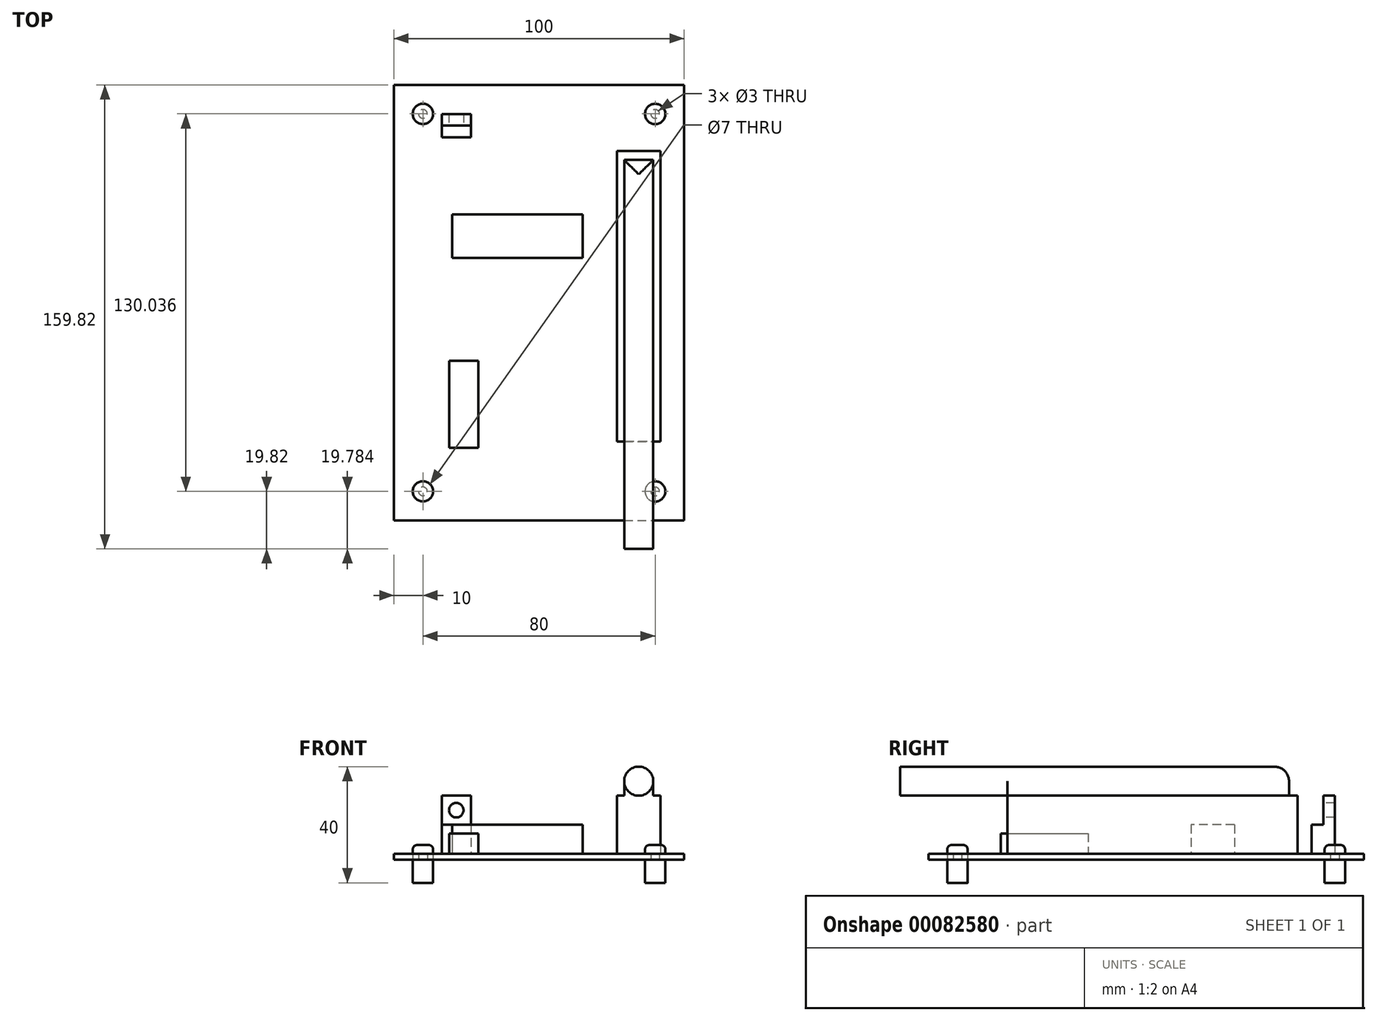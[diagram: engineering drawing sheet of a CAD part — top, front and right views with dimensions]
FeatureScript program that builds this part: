
annotation { "Feature Type Name" : "Feature", "Feature Type Description" : "" }
export const myFeature = defineFeature(function(context is Context, id is Id, definition is map)
    precondition{}
    {
        {
            var Q0;
            Q0=qCreatedBy(makeId("Top.planeOp"),FACE);
            var sketch = newSketch(context, id + "F0", { "sketchPlane" : qUnion([Q0])});
            skLineSegment(sketch, "E0.bottom", {"start": v(0, 0) * mm, "end": v(100, 0) * mm});
            skLineSegment(sketch, "E0.top", {"start": v(0, 150) * mm, "end": v(100, 150) * mm});
            skLineSegment(sketch, "E0.left", {"start": v(0, 0) * mm, "end": v(0, 150) * mm});
            skLineSegment(sketch, "E0.right", {"start": v(100, 0) * mm, "end": v(100, 150) * mm});
            skCircle(sketch, "E1", {"center": v(10, 10) * mm, "radius": 1.5 * mm});
            skCircle(sketch, "E2", {"center": v(10, 140) * mm, "radius": 1.5 * mm});
            skCircle(sketch, "E3", {"center": v(90, 9.96) * mm, "radius": 1.5 * mm});
            skCircle(sketch, "E4", {"center": v(90, 140) * mm, "radius": 1.5 * mm});
            skCircle(sketch, "E5", {"center": v(10, 10) * mm, "radius": 3.5 * mm});
            skSolve(sketch);
        }
        {
            var Q0;
            Q0=makeQuery(id+"F0.imprint","IMPRINT",FACE,{"disambiguationData":[TD([[makeQuery(id+"F0.imprint","IMPRINT",EDGE,{"derivedFrom":sQuery(id+"F0.wireOp",EDGE,"E0.bottom")}),1.0]])]});
            var Q1;
            Q1=makeQuery(id+"F0.imprint","IMPRINT",FACE,{"disambiguationData":[TD([[makeQuery(id+"F0.imprint","IMPRINT",EDGE,{"derivedFrom":sQuery(id+"F0.wireOp",EDGE,"E1")}),-1.0]])]});
            extrude(context, id + "F1", {"entities" : qUnion([Q0, Q1]), "depth" : 2 * mm});
        }
        {
            var Q0;
            Q0=makeQuery(id+"F1.opExtrude","CAP_FACE",FACE,{"disambiguationData":[OSD([sQuery(id+"F0.wireOp",EDGE,"E0.bottom"),sQuery(id+"F0.wireOp",EDGE,"E0.top"),sQuery(id+"F0.wireOp",EDGE,"E0.left"),sQuery(id+"F0.wireOp",EDGE,"E0.right"),sQuery(id+"F0.wireOp",EDGE,"E1"),sQuery(id+"F0.wireOp",EDGE,"E2"),sQuery(id+"F0.wireOp",EDGE,"E3"),sQuery(id+"F0.wireOp",EDGE,"E4")])],"isStart":false});
            var sketch = newSketch(context, id + "F2", { "sketchPlane" : qUnion([Q0])});
            skLineSegment(sketch, "E6.bottom", {"start": v(19.05, 24.96) * mm, "end": v(29.05, 24.96) * mm});
            skLineSegment(sketch, "E6.top", {"start": v(19.05, 54.96) * mm, "end": v(29.05, 54.96) * mm});
            skLineSegment(sketch, "E6.left", {"start": v(19.05, 24.96) * mm, "end": v(19.05, 54.96) * mm});
            skLineSegment(sketch, "E6.right", {"start": v(29.05, 24.96) * mm, "end": v(29.05, 54.96) * mm});
            skLineSegment(sketch, "E7.bottom", {"start": v(20, 105.4) * mm, "end": v(65, 105.4) * mm});
            skLineSegment(sketch, "E7.top", {"start": v(20, 90.4) * mm, "end": v(65, 90.4) * mm});
            skLineSegment(sketch, "E7.left", {"start": v(20, 105.4) * mm, "end": v(20, 90.4) * mm});
            skLineSegment(sketch, "E7.right", {"start": v(65, 105.4) * mm, "end": v(65, 90.4) * mm});
            skLineSegment(sketch, "E8.bottom", {"start": v(16.48, 139.98) * mm, "end": v(26.48, 139.98) * mm});
            skLineSegment(sketch, "E8.top", {"start": v(16.48, 131.98) * mm, "end": v(26.48, 131.98) * mm});
            skLineSegment(sketch, "E8.left", {"start": v(16.48, 139.98) * mm, "end": v(16.48, 131.98) * mm});
            skLineSegment(sketch, "E8.right", {"start": v(26.48, 139.98) * mm, "end": v(26.48, 131.98) * mm});
            skLineSegment(sketch, "E9.top", {"start": v(16.48, 135.98) * mm, "end": v(26.48, 135.98) * mm});
            skLineSegment(sketch, "E9.left", {"start": v(16.48, 139.98) * mm, "end": v(16.48, 135.98) * mm});
            skLineSegment(sketch, "E9.right", {"start": v(26.48, 139.98) * mm, "end": v(26.48, 135.98) * mm});
            skLineSegment(sketch, "E10.bottom", {"start": v(91.82, 127.18) * mm, "end": v(76.82, 127.18) * mm});
            skLineSegment(sketch, "E10.top", {"start": v(91.82, 27.18) * mm, "end": v(76.82, 27.18) * mm});
            skLineSegment(sketch, "E10.left", {"start": v(91.82, 127.18) * mm, "end": v(91.82, 27.18) * mm});
            skLineSegment(sketch, "E10.right", {"start": v(76.82, 127.18) * mm, "end": v(76.82, 27.18) * mm});
            skSolve(sketch);
        }
        {
            var Q0;
            Q0=makeQuery(id+"F2.imprint","IMPRINT",FACE,{"disambiguationData":[TD([[makeQuery(id+"F2.imprint","IMPRINT",EDGE,{"derivedFrom":sQuery(id+"F2.wireOp",EDGE,"E7.bottom")}),-1.0]])]});
            var Q1;
            Q1=makeQuery(id+"F2.imprint","IMPRINT",FACE,{"disambiguationData":[TD([[makeQuery(id+"F2.imprint","IMPRINT",EDGE,{"derivedFrom":sQuery(id+"F2.wireOp",EDGE,"E8.top")}),1.0]])]});
            var Q2;
            Q2=makeQuery(id+"F2.imprint","IMPRINT",FACE,{"disambiguationData":[TD([[makeQuery(id+"F2.imprint","IMPRINT",EDGE,{"derivedFrom":sQuery(id+"F2.wireOp",EDGE,"E8.bottom")}),-1.0]])]});
            var Q3;
            Q3=makeQuery(id+"F2.imprint","IMPRINT",FACE,{"disambiguationData":[TD([[makeQuery(id+"F2.imprint","IMPRINT",EDGE,{"derivedFrom":sQuery(id+"F2.wireOp",EDGE,"E10.bottom")}),1.0]])]});
            extrude(context, id + "F3", {"entities" : qUnion([Q0, Q1, Q2, Q3]), "depth" : 10 * mm});
        }
        {
            var Q0;
            Q0=makeQuery(id+"F2.imprint","IMPRINT",FACE,{"disambiguationData":[TD([[makeQuery(id+"F2.imprint","IMPRINT",EDGE,{"derivedFrom":sQuery(id+"F2.wireOp",EDGE,"E8.bottom")}),-1.0]])]});
            extrude(context, id + "F4", {"entities" : qUnion([Q0]), "operationType" : NewBodyOperationType.ADD, "depth" : 20 * mm});
        }
        {
            var Q0;
            Q0=makeQuery(id+"F2.imprint","IMPRINT",FACE,{"disambiguationData":[TD([[makeQuery(id+"F2.imprint","IMPRINT",EDGE,{"derivedFrom":sQuery(id+"F2.wireOp",EDGE,"E6.bottom")}),1.0]])]});
            extrude(context, id + "F5", {"entities" : qUnion([Q0]), "depth" : 7 * mm});
        }
        {
            var Q0;
            Q0=makeQuery(id+"F4.opExtrude","SWEPT_FACE",FACE,{"disambiguationData":[OSD([sQuery(id+"F2.wireOp",EDGE,"E9.top")])]});
            var sketch = newSketch(context, id + "F6", { "sketchPlane" : qUnion([Q0])});
            skCircle(sketch, "E11", {"center": v(21.48, 17) * mm, "radius": 2.5 * mm});
            skPoint(sketch, "E11.centerSnap0", {"position": v(26.48, 17) * mm});
            skPoint(sketch, "E11.centerSnap1", {"position": v(21.48, 22) * mm});
            skSolve(sketch);
        }
        {
            var Q0;
            Q0=qSketchRegion(id+"F6",true);
            extrude(context, id + "F7", {"entities" : qUnion([Q0]), "operationType" : NewBodyOperationType.REMOVE, "oppositeDirection" : true, "depth" : 25 * mm});
        }
        {
            var Q0;
            Q0=makeQuery(id+"F3.opExtrude","CAP_FACE",FACE,{"disambiguationData":[OSD([sQuery(id+"F2.wireOp",EDGE,"E10.bottom"),sQuery(id+"F2.wireOp",EDGE,"E10.top"),sQuery(id+"F2.wireOp",EDGE,"E10.left"),sQuery(id+"F2.wireOp",EDGE,"E10.right")])],"isStart":false});
            extrude(context, id + "F8", {"entities" : qUnion([Q0]), "operationType" : NewBodyOperationType.ADD, "depth" : 10 * mm});
        }
        {
            var Q0;
            Q0=makeQuery(id+"F8.opExtrude","CAP_FACE",FACE,{"disambiguationData":[OSD([sQuery(id+"F2.wireOp",EDGE,"E10.bottom"),sQuery(id+"F2.wireOp",EDGE,"E10.top"),sQuery(id+"F2.wireOp",EDGE,"E10.left"),sQuery(id+"F2.wireOp",EDGE,"E10.right")])],"isStart":false});
            var sketch = newSketch(context, id + "F9", { "sketchPlane" : qUnion([Q0])});
            skLineSegment(sketch, "E12.bottom", {"start": v(79.32, 124.18) * mm, "end": v(89.32, 124.18) * mm});
            skLineSegment(sketch, "E12.top", {"start": v(79.32, 30.18) * mm, "end": v(89.32, 30.18) * mm});
            skLineSegment(sketch, "E12.left", {"start": v(79.32, 124.18) * mm, "end": v(79.32, 30.18) * mm});
            skLineSegment(sketch, "E12.right", {"start": v(89.32, 124.18) * mm, "end": v(89.32, 30.18) * mm});
            skLineSegment(sketch, "E13", {"start": v(79.32, 124.18) * mm, "end": v(76.82, 127.18) * mm});
            skLineSegment(sketch, "E14", {"start": v(89.32, 124.18) * mm, "end": v(91.82, 127.18) * mm});
            skLineSegment(sketch, "E15", {"start": v(89.32, 30.18) * mm, "end": v(91.82, 27.18) * mm});
            skLineSegment(sketch, "E16", {"start": v(76.82, 27.18) * mm, "end": v(79.32, 30.18) * mm});
            skLineSegment(sketch, "E17.bottom", {"start": v(79.32, 124.18) * mm, "end": v(76.82, 124.18) * mm});
            skLineSegment(sketch, "E17.top", {"start": v(79.32, 127.18) * mm, "end": v(76.82, 127.18) * mm});
            skLineSegment(sketch, "E17.left", {"start": v(79.32, 124.18) * mm, "end": v(79.32, 127.18) * mm});
            skLineSegment(sketch, "E17.right", {"start": v(76.82, 124.18) * mm, "end": v(76.82, 127.18) * mm});
            skSolve(sketch);
        }
        {
            var Q0;
            Q0=makeQuery(id+"F9.imprint","IMPRINT",FACE,{"disambiguationData":[TD([[makeQuery(id+"F9.imprint","IMPRINT",EDGE,{"derivedFrom":sQuery(id+"F9.wireOp",EDGE,"E12.bottom")}),-1.0]])]});
            extrude(context, id + "F10", {"entities" : qUnion([Q0]), "operationType" : NewBodyOperationType.ADD, "depth" : 10 * mm});
        }
        {
            var Q0;
            Q0=makeQuery(id+"F10.opExtrude","CAP_EDGE",EDGE,{"disambiguationData":[OSD([sQuery(id+"F9.wireOp",EDGE,"E12.right")])],"isStart":false});
            var Q1;
            Q1=makeQuery(id+"F10.opExtrude","CAP_EDGE",EDGE,{"disambiguationData":[OSD([sQuery(id+"F9.wireOp",EDGE,"E12.left")])],"isStart":false});
            var Q2;
            Q2=makeQuery(id+"F10.opExtrude","CAP_EDGE",EDGE,{"disambiguationData":[OSD([sQuery(id+"F9.wireOp",EDGE,"E12.bottom")])],"isStart":false});
            fillet(context, id + "F11", {"entities" : qUnion([Q0, Q1, Q2]), "radius" : 5 * mm, "tangentPropagation" : true, "allowEdgeOverflow" : false});
        }
        {
            var Q0;
            Q0=makeQuery(id+"F10.opExtrude","SWEPT_FACE",FACE,{"disambiguationData":[OSD([sQuery(id+"F9.wireOp",EDGE,"E12.top")])]});
            var Q1;
            Q1=makeQuery(id+"F1.opExtrude","SWEPT_FACE",FACE,{"disambiguationData":[OSD([sQuery(id+"F0.wireOp",EDGE,"E0.bottom")])]});
            extrude(context, id + "F12", {"entities" : qUnion([Q0]), "operationType" : NewBodyOperationType.ADD, "endBoundEntityFace" : qUnion([Q1]), "depth" : 40 * mm});
        }
        {
            var Q0;
            Q0=makeQuery(id+"F12.boolean.opBoolean","SPLIT",EDGE,{"derivedFrom":makeQuery(id+"F12.opExtrude","SWEPT_EDGE",EDGE,{"disambiguationData":[OSD([sQuery(id+"F9.wireOp",EDGE,"E12.top"),sQuery(id+"F9.wireOp",EDGE,"E12.right"),sQuery(id+"F9.wireOp",EDGE,"E15")])]})});
            var Q1;
            Q1=makeQuery(id+"F12.boolean.opBoolean","SPLIT",EDGE,{"derivedFrom":makeQuery(id+"F12.opExtrude","SWEPT_EDGE",EDGE,{"disambiguationData":[OSD([sQuery(id+"F9.wireOp",EDGE,"E12.top"),sQuery(id+"F9.wireOp",EDGE,"E12.left"),sQuery(id+"F9.wireOp",EDGE,"E16")])]})});
            fillet(context, id + "F13", {"entities" : qUnion([Q0, Q1]), "radius" : 5 * mm, "tangentPropagation" : true, "allowEdgeOverflow" : false});
        }
        {
            var Q0;
            Q0=makeQuery(id+"F0.imprint","IMPRINT",FACE,{"disambiguationData":[TD([[makeQuery(id+"F0.imprint","IMPRINT",EDGE,{"derivedFrom":sQuery(id+"F0.wireOp",EDGE,"E1")}),-1.0]])]});
            var Q1;
            Q1=makeQuery(id+"F0.imprint","IMPRINT",FACE,{"disambiguationData":[TD([[makeQuery(id+"F0.imprint","IMPRINT",EDGE,{"derivedFrom":sQuery(id+"F0.wireOp",EDGE,"E1")}),1.0]])]});
            extrude(context, id + "F14", {"entities" : qUnion([Q0, Q1]), "depth" : 5 * mm});
        }
        {
            var Q0;
            Q0=makeQuery(id+"F0.imprint","IMPRINT",FACE,{"disambiguationData":[TD([[makeQuery(id+"F0.imprint","IMPRINT",EDGE,{"derivedFrom":sQuery(id+"F0.wireOp",EDGE,"E1")}),-1.0]])]});
            extrude(context, id + "F15", {"entities" : qUnion([Q0]), "operationType" : NewBodyOperationType.REMOVE, "depth" : 2 * mm});
        }
        {
            var Q0;
            Q0=makeQuery(id+"F14.opExtrude","CAP_EDGE",EDGE,{"disambiguationData":[OSD([sQuery(id+"F0.wireOp",EDGE,"E5")])],"isStart":false});
            fillet(context, id + "F16", {"entities" : qUnion([Q0]), "radius" : 1.5 * mm, "tangentPropagation" : true, "allowEdgeOverflow" : false});
        }
        {
            var Q0;
            Q0=makeQuery(id+"F0.imprint","IMPRINT",FACE,{"disambiguationData":[TD([[makeQuery(id+"F0.imprint","IMPRINT",EDGE,{"derivedFrom":sQuery(id+"F0.wireOp",EDGE,"E1")}),-1.0]])]});
            var Q1;
            Q1=makeQuery(id+"F0.imprint","IMPRINT",FACE,{"disambiguationData":[TD([[makeQuery(id+"F0.imprint","IMPRINT",EDGE,{"derivedFrom":sQuery(id+"F0.wireOp",EDGE,"E1")}),1.0]])]});
            extrude(context, id + "F17", {"entities" : qUnion([Q0, Q1]), "operationType" : NewBodyOperationType.ADD, "oppositeDirection" : true, "depth" : 8 * mm});
        }
        {
            var Q0;
            Q0=makeQuery(id+"F14.opExtrude","SWEPT_BODY",BODY,{"disambiguationData":[OSD([sQuery(id+"F0.wireOp",EDGE,"E5")])]});
            var Q1;
            Q1=sQuery(id+"F0.wireOp",VERTEX,"E2.center");
            var Q2;
            Q2=sQuery(id+"F0.wireOp",VERTEX,"E5.center");
            var Q3;
            Q3=sQuery(id+"F0.wireOp",VERTEX,"E2.center");
            var Q4;
            Q4=sQuery(id+"F0.wireOp",VERTEX,"E5.center");
            transform(context, id + "F18", {"entities" : qUnion([Q0]), "transformType" : TransformType.TRANSLATION_ENTITY, "oppositeDirectionEntity" : true, "transformLine" : qUnion([Q1, Q2]), "makeCopy" : true});
        }
        {
            var Q0;
            Q0=makeQuery(id+"F14.opExtrude","SWEPT_BODY",BODY,{"disambiguationData":[OSD([sQuery(id+"F0.wireOp",EDGE,"E5")])]});
            var Q1;
            Q1=makeQuery(id+"F18.opPattern","COPY",BODY,{"derivedFrom":makeQuery(id+"F14.opExtrude","SWEPT_BODY",BODY,{"disambiguationData":[OSD([sQuery(id+"F0.wireOp",EDGE,"E5")])]}),"instanceName":"1"});
            var Q2;
            Q2=sQuery(id+"F0.wireOp",VERTEX,"E5.center");
            var Q3;
            Q3=sQuery(id+"F0.wireOp",VERTEX,"E3.center");
            transform(context, id + "F19", {"entities" : qUnion([Q0, Q1]), "transformType" : TransformType.TRANSLATION_ENTITY, "oppositeDirectionEntity" : false, "transformLine" : qUnion([Q2, Q3]), "makeCopy" : true});
        }
    });
